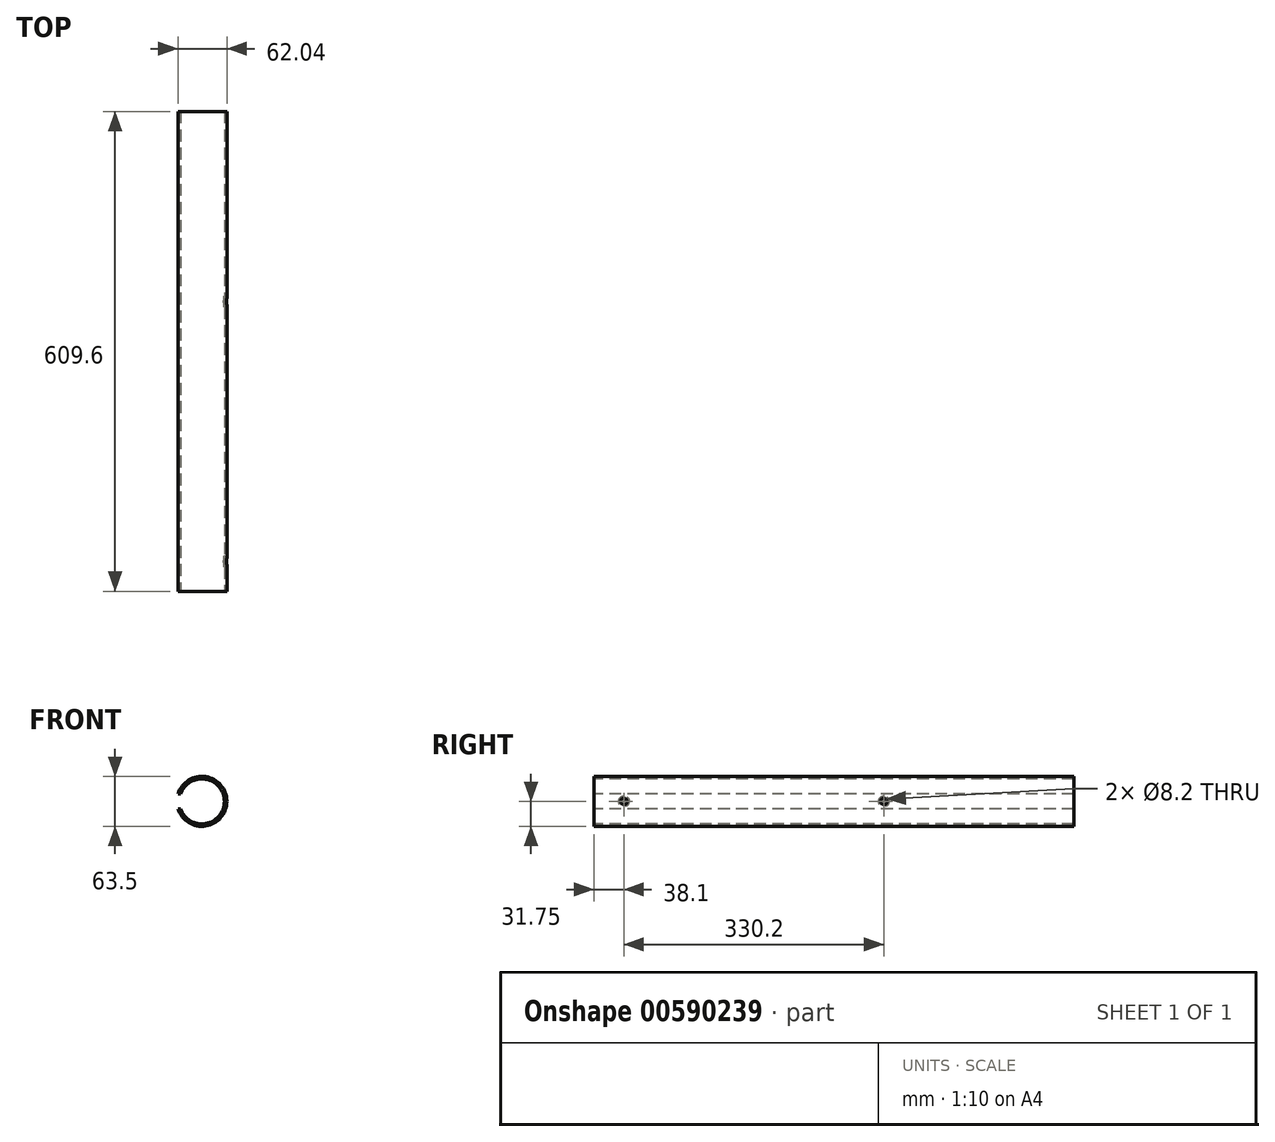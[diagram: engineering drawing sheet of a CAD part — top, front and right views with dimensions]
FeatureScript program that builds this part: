
annotation { "Feature Type Name" : "Feature", "Feature Type Description" : "" }
export const myFeature = defineFeature(function(context is Context, id is Id, definition is map)
    precondition{}
    {
        {
            var Q0;
            Q0=qCreatedBy(makeId("Front.planeOp"),FACE);
            var sketch = newSketch(context, id + "F0", { "sketchPlane" : qUnion([Q0])});
            skArc(sketch, "E0", {"start": v(-26.94, -9.53) * mm, "mid": v(28.58, 0) * mm, "end": v(-26.94, 9.53) * mm});
            skArc(sketch, "E1.0", {"start": v(-30.29, -9.52) * mm, "mid": v(31.75, 0) * mm, "end": v(-30.29, 9.53) * mm});
            skLineSegment(sketch, "E2.bottom", {"start": v(-30.29, 9.53) * mm, "end": v(-26.94, 9.53) * mm});
            skLineSegment(sketch, "E2.top", {"start": v(-30.29, -9.53) * mm, "end": v(-26.94, -9.53) * mm});
            skPoint(sketch, "E3.orphan", {"position": v(-52.43, 9.53) * mm});
            skPoint(sketch, "E4.orphan", {"position": v(-52.43, -9.53) * mm});
            skSolve(sketch);
        }
        {
            var Q0;
            Q0=makeQuery(id+"F0.imprint","IMPRINT",FACE,{"disambiguationData":[TD([[makeQuery(id+"F0.imprint","IMPRINT",EDGE,{"derivedFrom":sQuery(id+"F0.wireOp",EDGE,"E0")}),-1.0]])]});
            extrude(context, id + "F1", {"entities" : qUnion([Q0]), "oppositeDirection" : true, "depth" : 609.6 * mm, "offsetDistance" : 25.4 * mm});
        }
        {
            var Q0;
            Q0=qCreatedBy(makeId("Right.planeOp"),FACE);
            var sketch = newSketch(context, id + "F2", { "sketchPlane" : qUnion([Q0])});
            skLineSegment(sketch, "E5", {"start": v(0, 0) * mm, "end": v(38.1, 0) * mm, "construction": true});
            skLineSegment(sketch, "E6", {"start": v(38.1, 0) * mm, "end": v(368.3, 0) * mm, "construction": true});
            skCircle(sketch, "E7", {"center": v(38.1, 0) * mm, "radius": 4.1 * mm});
            skCircle(sketch, "E8", {"center": v(368.3, 0) * mm, "radius": 4.1 * mm});
            skSolve(sketch);
        }
        {
            var Q0;
            Q0=makeQuery(id+"F2.imprint","IMPRINT",FACE,{"disambiguationData":[TD([[makeQuery(id+"F2.imprint","IMPRINT",EDGE,{"derivedFrom":sQuery(id+"F2.wireOp",EDGE,"E7")}),1.0]])]});
            var Q1;
            Q1=makeQuery(id+"F2.imprint","IMPRINT",FACE,{"disambiguationData":[TD([[makeQuery(id+"F2.imprint","IMPRINT",EDGE,{"derivedFrom":sQuery(id+"F2.wireOp",EDGE,"E8")}),1.0]])]});
            extrude(context, id + "F3", {"entities" : qUnion([Q0, Q1]), "operationType" : NewBodyOperationType.REMOVE, "depth" : 35.05 * mm, "offsetDistance" : 25.4 * mm});
        }
        {
            var Q0;
            Q0=makeQuery(id+"F3.boolean.opBoolean","INTERSECT",EDGE,{"derivedFrom":[makeQuery(id+"F1.opExtrude","SWEPT_FACE",FACE,{"disambiguationData":[OSD([sQuery(id+"F0.wireOp",EDGE,"E0")])]}),makeQuery(id+"F3.opExtrude","SWEPT_FACE",FACE,{"disambiguationData":[OSD([sQuery(id+"F2.wireOp",EDGE,"E8")])]})]});
            chamfer(context, id + "F4", {"entities" : qUnion([Q0]), "chamferType" : ChamferType.OFFSET_ANGLE, "width" : 2.54 * mm, "oppositeDirection" : false, "angle" : 41 * degree, "tangentPropagation" : true});
        }
        {
            var Q0;
            Q0=makeQuery(id+"F3.boolean.opBoolean","INTERSECT",EDGE,{"derivedFrom":[makeQuery(id+"F1.opExtrude","SWEPT_FACE",FACE,{"disambiguationData":[OSD([sQuery(id+"F0.wireOp",EDGE,"E0")])]}),makeQuery(id+"F3.opExtrude","SWEPT_FACE",FACE,{"disambiguationData":[OSD([sQuery(id+"F2.wireOp",EDGE,"E7")])]})]});
            chamfer(context, id + "F5", {"entities" : qUnion([Q0]), "chamferType" : ChamferType.OFFSET_ANGLE, "width" : 2.54 * mm, "oppositeDirection" : false, "angle" : 41 * degree, "tangentPropagation" : true});
        }
    });
